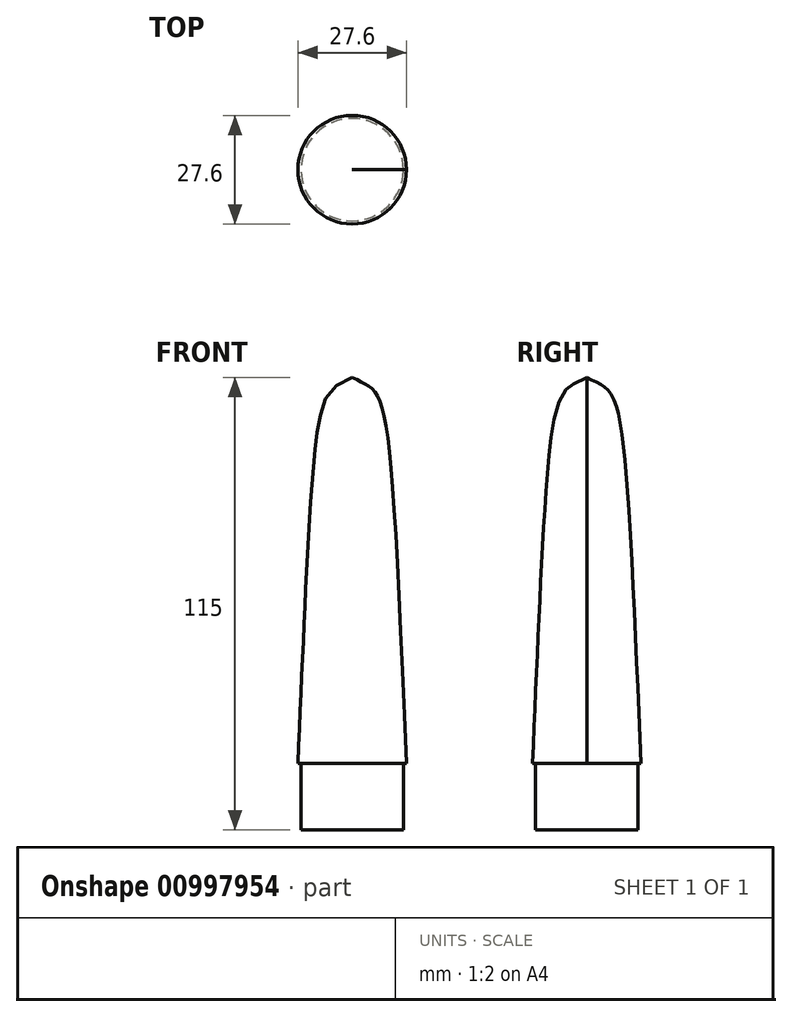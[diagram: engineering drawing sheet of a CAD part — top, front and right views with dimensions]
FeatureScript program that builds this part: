
annotation { "Feature Type Name" : "Feature", "Feature Type Description" : "" }
export const myFeature = defineFeature(function(context is Context, id is Id, definition is map)
    precondition{}
    {
        {
            var Q0;
            Q0=qCreatedBy(makeId("Front.planeOp"),FACE);
            var sketch = newSketch(context, id + "F0", { "sketchPlane" : qUnion([Q0])});
            skLineSegment(sketch, "E0", {"start": v(0, 0) * mm, "end": v(13, 0) * mm});
            skLineSegment(sketch, "E1", {"start": v(13, 0) * mm, "end": v(13, 17) * mm});
            skLineSegment(sketch, "E2", {"start": v(13, 17) * mm, "end": v(13.8, 17) * mm});
            skFitSpline(sketch, "E3", {"points": [v(13.8, 17) * mm, v(0, 115) * mm], "startDerivative": vector(-12.88, 296.33) * mm, "endDerivative": vector(-28.52, 14.27) * mm});
            skLineSegment(sketch, "E4", {"start": v(0, 115) * mm, "end": v(0, 0) * mm});
            skSolve(sketch);
        }
        {
            var Q0;
            Q0=makeQuery(id+"F0.imprint","IMPRINT",FACE,{"disambiguationData":[TD([[makeQuery(id+"F0.imprint","IMPRINT",EDGE,{"derivedFrom":sQuery(id+"F0.wireOp",EDGE,"E0")}),1.0]])]});
            var Q1;
            Q1=sQuery(id+"F0.wireOp",EDGE,"E4");
            revolve(context, id + "F1", {"surfaceOperationType" : NewSurfaceOperationType.NEW, "entities" : qUnion([Q0]), "axis" : qUnion([Q1]), "revolveType" : RevolveType.FULL});
        }
    });
